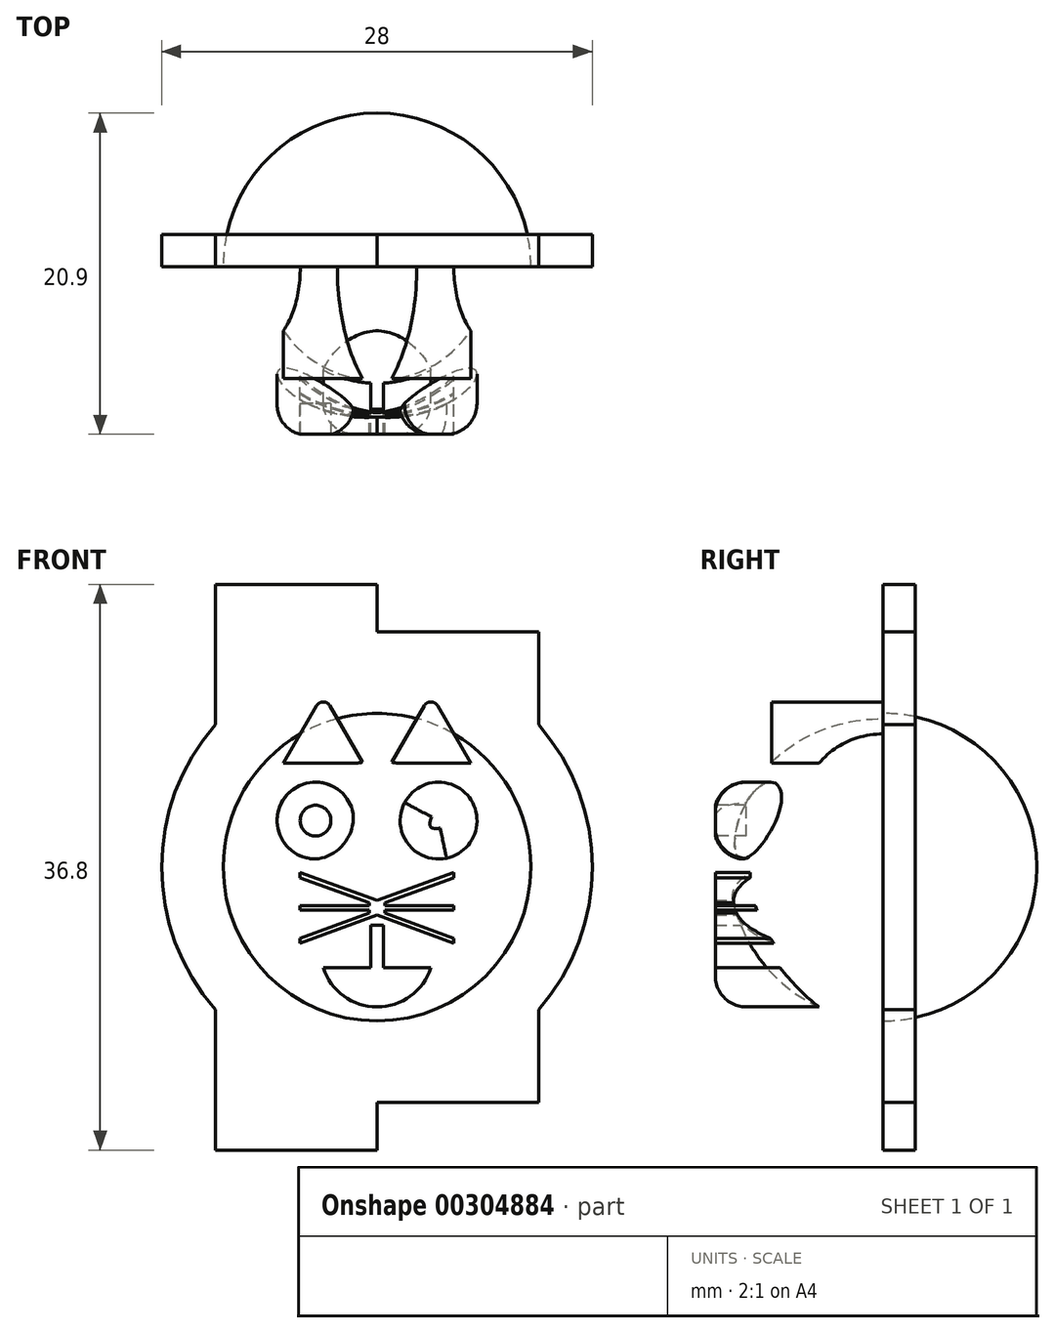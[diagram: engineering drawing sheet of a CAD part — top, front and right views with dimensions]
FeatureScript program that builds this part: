
annotation { "Feature Type Name" : "Feature", "Feature Type Description" : "" }
export const myFeature = defineFeature(function(context is Context, id is Id, definition is map)
    precondition{}
    {
        {
            var Q0;
            Q0=qCreatedBy(makeId("Front.planeOp"),FACE);
            var sketch = newSketch(context, id + "F0", { "sketchPlane" : qUnion([Q0])});
            skLineSegment(sketch, "E0", {"start": v(-10.5, 18.4) * mm, "end": v(-10.5, 9.26) * mm});
            skLineSegment(sketch, "E1", {"start": v(-10.5, 18.4) * mm, "end": v(0, 18.4) * mm});
            skLineSegment(sketch, "E2", {"start": v(0, 18.4) * mm, "end": v(0, 15.3) * mm});
            skLineSegment(sketch, "E3", {"start": v(0, 15.3) * mm, "end": v(10.5, 15.3) * mm});
            skLineSegment(sketch, "E4", {"start": v(10.5, 15.3) * mm, "end": v(10.5, 9.26) * mm});
            skLineSegment(sketch, "E5", {"start": v(-10.5, -9.26) * mm, "end": v(-10.5, -18.4) * mm});
            skLineSegment(sketch, "E6", {"start": v(-10.5, -18.4) * mm, "end": v(0, -18.4) * mm});
            skLineSegment(sketch, "E7", {"start": v(0, -18.4) * mm, "end": v(0, -15.3) * mm});
            skLineSegment(sketch, "E8", {"start": v(0, -15.3) * mm, "end": v(10.5, -15.3) * mm});
            skLineSegment(sketch, "E9", {"start": v(10.5, -15.3) * mm, "end": v(10.5, -9.26) * mm});
            skArc(sketch, "E10", {"start": v(-10.5, 9.26) * mm, "mid": v(-14, 0) * mm, "end": v(-10.5, -9.26) * mm});
            skArc(sketch, "E11", {"start": v(10.5, -9.26) * mm, "mid": v(14, 0) * mm, "end": v(10.5, 9.26) * mm});
            skSolve(sketch);
        }
        {
            var Q0;
            Q0=makeQuery(id+"F0.imprint","IMPRINT",FACE,{"disambiguationData":[TD([[makeQuery(id+"F0.imprint","IMPRINT",EDGE,{"derivedFrom":sQuery(id+"F0.wireOp",EDGE,"E0")}),1.0]])]});
            extrude(context, id + "F1", {"entities" : qUnion([Q0]), "depth" : 2.1 * mm});
        }
        {
            var Q0;
            Q0=makeQuery(id+"F1.opExtrude","CAP_FACE",FACE,{"disambiguationData":[OSD([sQuery(id+"F0.wireOp",EDGE,"E0"),sQuery(id+"F0.wireOp",EDGE,"E1"),sQuery(id+"F0.wireOp",EDGE,"E2"),sQuery(id+"F0.wireOp",EDGE,"E3"),sQuery(id+"F0.wireOp",EDGE,"E4"),sQuery(id+"F0.wireOp",EDGE,"E5"),sQuery(id+"F0.wireOp",EDGE,"E6"),sQuery(id+"F0.wireOp",EDGE,"E7"),sQuery(id+"F0.wireOp",EDGE,"E8"),sQuery(id+"F0.wireOp",EDGE,"E9"),sQuery(id+"F0.wireOp",EDGE,"E10"),sQuery(id+"F0.wireOp",EDGE,"E11")])],"isStart":false});
            var sketch = newSketch(context, id + "F2", { "sketchPlane" : qUnion([Q0])});
            skArc(sketch, "E12", {"start": v(10, 0) * mm, "mid": v(7.07, 7.07) * mm, "end": v(0, 10) * mm});
            skLineSegment(sketch, "E13", {"start": v(0, 0) * mm, "end": v(10, 0) * mm});
            skLineSegment(sketch, "E14", {"start": v(-26.98, 0) * mm, "end": v(28.17, 0) * mm});
            skArc(sketch, "E15", {"start": v(10, 0) * mm, "mid": v(0, 10) * mm, "end": v(-10, 0) * mm});
            skLineSegment(sketch, "E16", {"start": v(-10, 0) * mm, "end": v(10, 0) * mm});
            skSolve(sketch);
        }
        {
            var Q0;
            {var subQ1=sQuery(id+"F2.wireOp",EDGE,"E15");var subQ4=makeQuery(id+"F2.imprint","IMPRINT",VERTEX,{"derivedFrom":subQ1});Q0=makeQuery(id+"F2.imprint","IMPRINT",FACE,{"disambiguationData":[TD([[makeQuery(id+"F2.imprint","IMPRINT",EDGE,{"disambiguationData":[TD([[subQ4,1.0]])],"derivedFrom":subQ1}),1.0]])]});}
            var Q1;
            Q1=sQuery(id+"F2.wireOp",EDGE,"E14");
            revolve(context, id + "F3", {"operationType" : NewBodyOperationType.ADD, "entities" : qUnion([Q0]), "axis" : qUnion([Q1]), "revolveType" : RevolveType.FULL});
        }
        {
            var Q0;
            Q0=makeQuery(id+"F1.opExtrude","SWEPT_FACE",FACE,{"disambiguationData":[OSD([sQuery(id+"F0.wireOp",EDGE,"E4")])]});
            var sketch = newSketch(context, id + "F4", { "sketchPlane" : qUnion([Q0])});
            skLineSegment(sketch, "E17", {"start": v(0, 18) * mm, "end": v(13, 18) * mm});
            skLineSegment(sketch, "E18", {"start": v(13, 18) * mm, "end": v(13, -18) * mm});
            skLineSegment(sketch, "E19", {"start": v(13, -18) * mm, "end": v(0, -18) * mm});
            skLineSegment(sketch, "E20", {"start": v(0, -18) * mm, "end": v(0, 18) * mm});
            skSolve(sketch);
        }
        {
            var Q0;
            {var subQ4=sQuery(id+"F4.wireOp",EDGE,"E17");Q0=makeQuery(id+"F4.imprint","IMPRINT",FACE,{"disambiguationData":[TD([[makeQuery(id+"F4.imprint","IMPRINT",EDGE,{"derivedFrom":subQ4}),-1.0]])]});}
            extrude(context, id + "F5", {"entities" : qUnion([Q0]), "operationType" : NewBodyOperationType.REMOVE, "oppositeDirection" : true, "depth" : 60 * mm});
        }
        {
            var Q0;
            Q0=qCreatedBy(makeId("Front.planeOp"),FACE);
            var sketch = newSketch(context, id + "F6", { "sketchPlane" : qUnion([Q0])});
            skCircle(sketch, "E21", {"center": v(-4, 3.03) * mm, "radius": 2.5 * mm});
            skCircle(sketch, "E22", {"center": v(4, 3.03) * mm, "radius": 2.5 * mm});
            skLineSegment(sketch, "E23", {"start": v(0, -2.16) * mm, "end": v(5, -0.34) * mm});
            skLineSegment(sketch, "E24", {"start": v(0.5, -2.5) * mm, "end": v(5, -2.5) * mm});
            skLineSegment(sketch, "E25", {"start": v(5, -2.5) * mm, "end": v(5, -2.8) * mm});
            skLineSegment(sketch, "E26", {"start": v(5, -2.8) * mm, "end": v(0.5, -2.8) * mm});
            skLineSegment(sketch, "E27", {"start": v(5, -4.94) * mm, "end": v(0, -3.12) * mm});
            skLineSegment(sketch, "E28", {"start": v(0.5, -2.32) * mm, "end": v(5, -0.68) * mm});
            skLineSegment(sketch, "E29", {"start": v(5, -0.34) * mm, "end": v(5, -0.68) * mm});
            skLineSegment(sketch, "E30", {"start": v(5, -4.62) * mm, "end": v(5, -4.94) * mm});
            skLineSegment(sketch, "E31.MirrorCS", {"start": v(0, -2.16) * mm, "end": v(-5, -0.34) * mm});
            skLineSegment(sketch, "E32.MirrorCS", {"start": v(-0.5, -2.32) * mm, "end": v(-5, -0.68) * mm});
            skLineSegment(sketch, "E33.MirrorCS", {"start": v(-5, -0.34) * mm, "end": v(-5, -0.68) * mm});
            skLineSegment(sketch, "E34.MirrorCS", {"start": v(-0.5, -2.5) * mm, "end": v(-5, -2.5) * mm});
            skLineSegment(sketch, "E35.MirrorCS", {"start": v(-5, -2.8) * mm, "end": v(-0.5, -2.8) * mm});
            skLineSegment(sketch, "E36.MirrorCS", {"start": v(-5, -4.94) * mm, "end": v(0, -3.12) * mm});
            skLineSegment(sketch, "E37.MirrorCS", {"start": v(-5, -2.5) * mm, "end": v(-5, -2.8) * mm});
            skLineSegment(sketch, "E38.MirrorCS", {"start": v(-0.5, -2.98) * mm, "end": v(-5, -4.62) * mm});
            skLineSegment(sketch, "E39.MirrorCS", {"start": v(-5, -4.62) * mm, "end": v(-5, -4.94) * mm});
            skLineSegment(sketch, "E40", {"start": v(-0.4, -3.78) * mm, "end": v(0.4, -3.78) * mm});
            skLineSegment(sketch, "E41", {"start": v(0.4, -3.78) * mm, "end": v(0.4, -6.53) * mm});
            skLineSegment(sketch, "E42", {"start": v(-0.4, -3.78) * mm, "end": v(-0.4, -6.53) * mm});
            skLineSegment(sketch, "E43", {"start": v(-3.5, -6.53) * mm, "end": v(-0.4, -6.53) * mm});
            skArc(sketch, "E44", {"start": v(-3.5, -6.53) * mm, "mid": v(0, -9.1) * mm, "end": v(3.5, -6.53) * mm});
            skLineSegment(sketch, "E45.trimOffspring", {"start": v(0.4, -6.53) * mm, "end": v(3.5, -6.53) * mm});
            skLineSegment(sketch, "E46", {"start": v(0.5, -2.32) * mm, "end": v(0.5, -2.5) * mm});
            skLineSegment(sketch, "E47", {"start": v(-0.5, -2.32) * mm, "end": v(-0.5, -2.5) * mm});
            skPoint(sketch, "E48.orphan", {"position": v(0, -2.5) * mm});
            skLineSegment(sketch, "E49.trimOffspring", {"start": v(-0.5, -2.8) * mm, "end": v(-0.5, -2.98) * mm});
            skPoint(sketch, "E50.orphan", {"position": v(0, -2.8) * mm});
            skLineSegment(sketch, "E51.trimOffspring", {"start": v(0.5, -2.8) * mm, "end": v(0.5, -2.98) * mm});
            skLineSegment(sketch, "E52", {"start": v(5, -4.62) * mm, "end": v(0.5, -2.98) * mm});
            skSolve(sketch);
        }
        {
            var Q0;
            Q0=qCreatedBy(makeId("Front.planeOp"),FACE);
            var sketch = newSketch(context, id + "F7", { "sketchPlane" : qUnion([Q0])});
            skCircle(sketch, "E53.cCircle", {"center": v(3.5, 8.25) * mm, "radius": 1.5 * mm, "construction": true});
            skLineSegment(sketch, "E53.0", {"start": v(6.1, 6.75) * mm, "end": v(0.9, 6.75) * mm});
            skLineSegment(sketch, "E53.1", {"start": v(0.9, 6.75) * mm, "end": v(3.5, 11.25) * mm});
            skLineSegment(sketch, "E53.2", {"start": v(3.5, 11.25) * mm, "end": v(6.1, 6.75) * mm});
            skPoint(sketch, "E53.0.midPoint", {"position": v(3.5, 6.75) * mm});
            skLineSegment(sketch, "E54.MirrorCS", {"start": v(-0.9, 6.75) * mm, "end": v(-3.5, 11.25) * mm});
            skLineSegment(sketch, "E55.MirrorCS", {"start": v(-3.5, 11.25) * mm, "end": v(-6.1, 6.75) * mm});
            skLineSegment(sketch, "E56.MirrorCS", {"start": v(-6.1, 6.75) * mm, "end": v(-0.9, 6.75) * mm});
            skSolve(sketch);
        }
        {
            var Q0;
            Q0 = qSketchRegion(id + "F6", true);
            extrude(context, id + "F8", {"entities" : qUnion([Q0]), "operationType" : NewBodyOperationType.ADD, "depth" : 13 * mm});
        }
        {
            var Q0;
            Q0 = qSketchRegion(id + "F7", true);
            extrude(context, id + "F9", {"entities" : qUnion([Q0]), "operationType" : NewBodyOperationType.ADD, "depth" : 9.35 * mm});
        }
        {
            var Q0;
            Q0=makeQuery(id+"F8.opExtrude","CAP_FACE",FACE,{"disambiguationData":[OSD([sQuery(id+"F6.wireOp",EDGE,"E21")])],"isStart":false});
            var sketch = newSketch(context, id + "F10", { "sketchPlane" : qUnion([Q0])});
            skCircle(sketch, "E57", {"center": v(-4, 3.03) * mm, "radius": 1 * mm});
            skCircle(sketch, "E58.MirrorC", {"center": v(4, 3.03) * mm, "radius": 1 * mm});
            skSolve(sketch);
        }
        {
            var Q0;
            Q0=makeQuery(id+"F10.imprint","IMPRINT",FACE,{"disambiguationData":[TD([[makeQuery(id+"F10.imprint","IMPRINT",EDGE,{"derivedFrom":sQuery(id+"F10.wireOp",EDGE,"E57")}),1.0]])]});
            var Q1;
            Q1=makeQuery(id+"F10.imprint","IMPRINT",FACE,{"disambiguationData":[TD([[makeQuery(id+"F10.imprint","IMPRINT",EDGE,{"derivedFrom":sQuery(id+"F10.wireOp",EDGE,"E58.MirrorC")}),-1.0]])]});
            extrude(context, id + "F11", {"entities" : qUnion([Q0, Q1]), "operationType" : NewBodyOperationType.REMOVE, "oppositeDirection" : true, "depth" : 2 * mm});
        }
        {
            var Q0;
            Q0=makeQuery(id+"F8.opExtrude","CAP_EDGE",EDGE,{"disambiguationData":[OSD([sQuery(id+"F6.wireOp",EDGE,"E21")])],"isStart":false});
            var Q1;
            Q1=makeQuery(id+"F8.opExtrude","CAP_EDGE",EDGE,{"disambiguationData":[OSD([sQuery(id+"F6.wireOp",EDGE,"E22")])],"isStart":false});
            var Q2;
            Q2=makeQuery(id+"F8.opExtrude","CAP_EDGE",EDGE,{"disambiguationData":[OSD([sQuery(id+"F6.wireOp",EDGE,"E44")])],"isStart":false});
            fillet(context, id + "F12", {"entities" : qUnion([Q0, Q1, Q2]), "radius" : 2 * mm, "tangentPropagation" : true, "allowEdgeOverflow" : false});
        }
        {
            var Q0;
            Q0=makeQuery(id+"F9.opExtrude","SWEPT_EDGE",EDGE,{"disambiguationData":[OSD([sQuery(id+"F7.wireOp",EDGE,"E54.MirrorCS"),sQuery(id+"F7.wireOp",EDGE,"E55.MirrorCS")])]});
            var Q1;
            Q1=makeQuery(id+"F9.opExtrude","SWEPT_EDGE",EDGE,{"disambiguationData":[OSD([sQuery(id+"F7.wireOp",EDGE,"E53.1"),sQuery(id+"F7.wireOp",EDGE,"E53.2")])]});
            fillet(context, id + "F13", {"entities" : qUnion([Q0, Q1]), "radius" : 0.5 * mm, "tangentPropagation" : true, "allowEdgeOverflow" : false});
        }
    });
